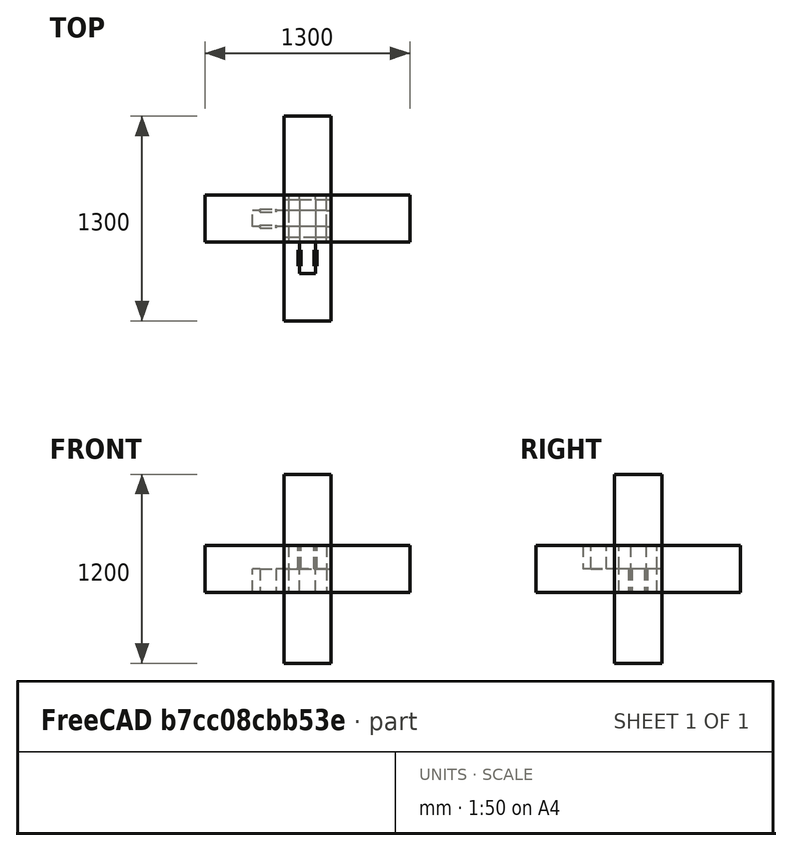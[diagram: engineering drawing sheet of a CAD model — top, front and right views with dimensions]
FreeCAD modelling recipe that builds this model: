
FCSTD DOCUMENT  (FreeCAD 0.19R16207 (Git))
Label: EMENDA
License: All rights reserved
LicenseURL: http://en.wikipedia.org/wiki/All_rights_reserved
objects: Part::FeaturePython×9, Part::Feature×7, Part::Cut×7, Part::Box×5, Part::MultiFuse×2, Part::Compound×1
note: 31 computed .brp shape members not serialized (recipe doc carries the construction recipe); baked Part::Feature solids carry a one-line shape summary decoded from their .brp

FEATURE [Part::Box] Box  label="Cube"
  AttacherType = Attacher::AttachEngine3D
  Height = 300
  Length = 300
  Placement = pos=(-150,0,-150) rot=(0,0,1;0rad)
  Width = 500
FEATURE [Part::Box] Box001  label="Cube001"
  AttacherType = Attacher::AttachEngine3D
  Height = 150
  Length = 100
  Placement = pos=(50,-30,0) rot=(0,0,1;0rad)
  Width = 30
FEATURE [Part::FeaturePython] Clone  label="Cube002"  # Draft clone (typed FeaturePython)
  AttacherType = Attacher::AttachEngine3D
  Fuse = false
  Objects = -> [Box001]
  Placement = pos=(-150,-30,0) rot=(0,0,1;0rad)
  Scale = (1,1,1)
FEATURE [Part::FeaturePython] Clone001  label="Cube003"  # Draft clone (typed FeaturePython)
  AttacherType = Attacher::AttachEngine3D
  Fuse = false
  Objects = -> [Clone]
  Placement = pos=(-50,-30,-150) rot=(0,0,1;0rad)
  Scale = (1,1,1)
FEATURE [Part::MultiFuse] Fusion
  Shapes = -> [Box,Box001,Clone,Clone001]
FEATURE [Part::Feature] Fusion001
  shape: bbox 300 x 530 x 300 mm, 18 faces (baked)
FEATURE [Part::FeaturePython] Clone002  label="Fusion002"  # Draft clone (typed FeaturePython)
  AttacherType = Attacher::AttachEngine3D
  Fuse = false
  Objects = -> [Fusion001]
  Placement = pos=(-150,-150,0) rot=(-0.707107,0.707107,0;3.14159rad)
  Scale = (1,1,1)
FEATURE [Part::Box] Box002  label="Cube004"
  AttacherType = Attacher::AttachEngine3D
  Height = 150
  Length = 100
  Placement = pos=(-50,1.84e-14,150) rot=(1,0,0;3.14159rad)
  Width = 500
FEATURE [Part::MultiFuse] Fusion002  label="Fusion003"
  Shapes = -> [Fusion001,Box002]
FEATURE [Part::Feature] Fusion002001  label="Fusion004"
  shape: bbox 300 x 1000 x 300 mm, 18 faces (baked)
FEATURE [Part::Box] Box003  label="Cube005"
  AttacherType = Attacher::AttachEngine3D
  Height = 150
  Length = 20
  Placement = pos=(40,-450,0) rot=(0,0,1;0rad)
  Width = 100
FEATURE [Part::FeaturePython] Clone003  label="Cube006"  # Draft clone (typed FeaturePython)
  AttacherType = Attacher::AttachEngine3D
  Fuse = false
  Objects = -> [Box003]
  Placement = pos=(-60,-450,0) rot=(0,0,1;0rad)
  Scale = (1,1,1)
FEATURE [Part::Compound] Compound
  Links = -> [Box003,Clone003]
FEATURE [Part::Cut] Cut  label="M1"
  Base = -> Fusion002001
  Tool = -> Compound
FEATURE [Part::Feature] Compound001  label="M5"
  shape: bbox 120 x 100 x 150 mm, 12 faces, 2 solids (baked)
FEATURE [Part::FeaturePython] Clone004  label="Cut001"  # Draft clone (typed FeaturePython)
  AttacherType = Attacher::AttachEngine3D
  Fuse = false
  Objects = -> [Cut]
  Placement = pos=(150,-150,1.84e-14) rot=(-0.707107,-0.707107,0;3.14159rad)
  Scale = (1,1,1)
FEATURE [Part::Cut] Cut001  label="Cut002"
  Base = -> Clone002
  Tool = -> Clone004
FEATURE [Part::FeaturePython] Clone005  label="Compound002"  # Draft clone (typed FeaturePython)
  AttacherType = Attacher::AttachEngine3D
  Fuse = false
  Objects = -> [Compound001]
  Placement = pos=(150,-150,1.84e-14) rot=(0.707107,0.707107,0;3.14159rad)
  Scale = (1,1,1)
FEATURE [Part::Cut] Cut002  label="M2"
  Base = -> Cut001
  Tool = -> Clone005
FEATURE [Part::FeaturePython] Clone006  label="M3"  # Draft clone (typed FeaturePython)
  AttacherType = Attacher::AttachEngine3D
  Fuse = false
  Objects = -> [Cut]
  Placement = pos=(150,-150,0) rot=(-0.707107,-0.707107,0;3.14159rad)
  Scale = (1,1,1)
FEATURE [Part::FeaturePython] Clone007  label="M4"  # Draft clone (typed FeaturePython)
  AttacherType = Attacher::AttachEngine3D
  Fuse = false
  Objects = -> [Cut002]
  Placement = pos=(150,-150,4.71e-14) rot=(-0.707107,-0.707107,0;3.14159rad)
  Scale = (1,1,1)
FEATURE [Part::FeaturePython] Clone008  label="M6"  # Draft clone (typed FeaturePython)
  AttacherType = Attacher::AttachEngine3D
  Fuse = false
  Objects = -> [Compound001]
  Placement = pos=(-650,-150,6.66e-14) rot=(0.707107,-0.707107,0;3.14159rad)
  Scale = (1,1,1)
FEATURE [Part::Box] Box004  label="Cube007"
  AttacherType = Attacher::AttachEngine3D
  Height = 1200
  Length = 300
  Placement = pos=(-150,-300,-600) rot=(0,0,1;0rad)
  Width = 300
FEATURE [Part::Cut] Cut003
  Base = -> Box004
  Tool = -> Cut
FEATURE [Part::Cut] Cut004
  Base = -> Cut003
  Tool = -> Cut002
FEATURE [Part::Cut] Cut005
  Base = -> Cut004
  Tool = -> Clone006
FEATURE [Part::Cut] Cut006
  Base = -> Cut005
  Tool = -> Clone007
FEATURE [Part::Feature] Cut007  label="M007"
  shape: bbox 300 x 1000 x 300 mm, 26 faces (baked)
FEATURE [Part::Feature] Cut002001  label="M008"
  shape: bbox 530 x 300 x 300 mm, 31 faces (baked)
FEATURE [Part::Feature] Clone006001  label="M009"
  shape: bbox 1000 x 300 x 300 mm, 26 faces (baked)
FEATURE [Part::Feature] Clone007_rev  label="M4 (Rev)"
  Placement = pos=(150,-150,4.71e-14) rot=(0.707107,0.707107,0;3.14159rad)
  shape: bbox 300 x 530 x 300 mm, 31 faces (baked)
